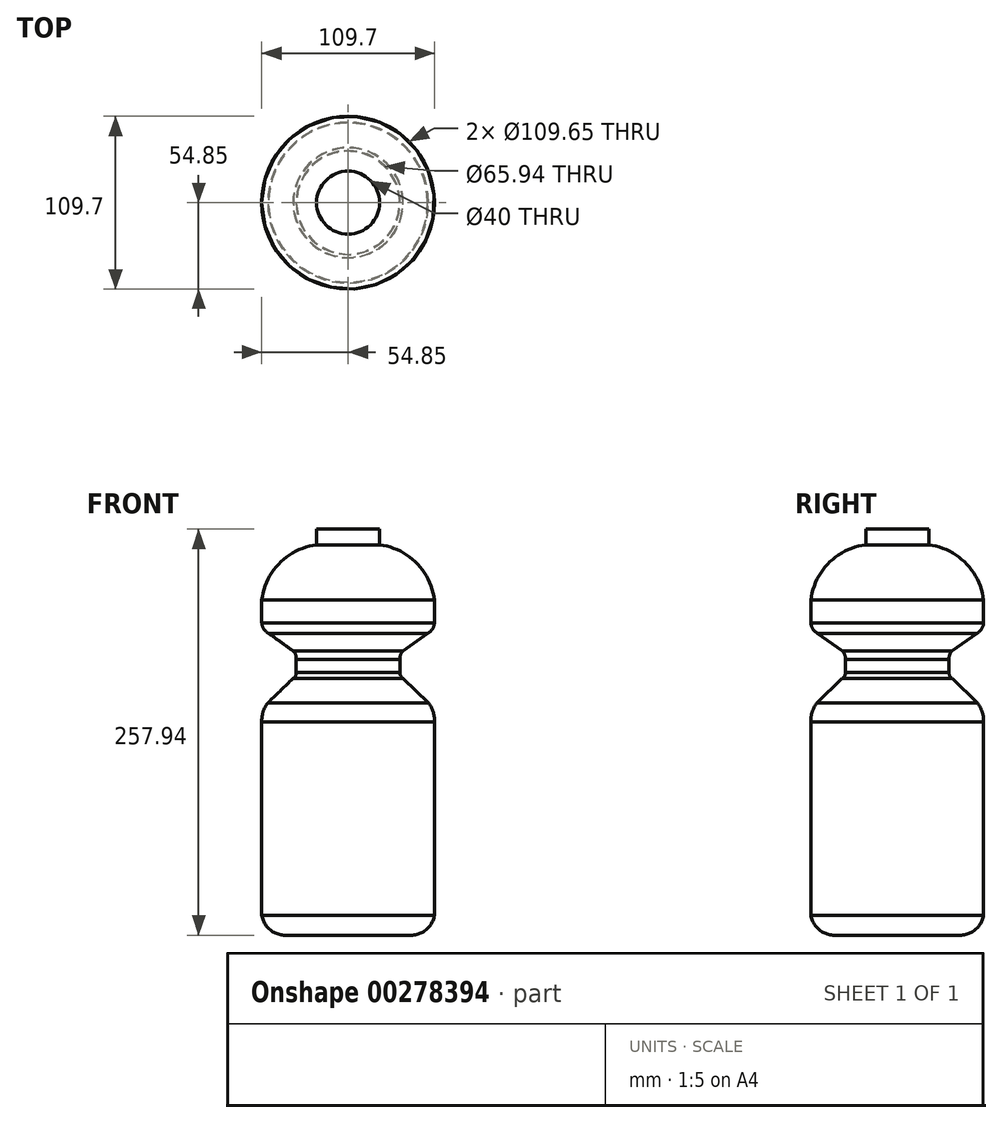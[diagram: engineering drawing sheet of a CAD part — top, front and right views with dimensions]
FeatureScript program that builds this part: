
annotation { "Feature Type Name" : "Feature", "Feature Type Description" : "" }
export const myFeature = defineFeature(function(context is Context, id is Id, definition is map)
    precondition{}
    {
        {
            var Q0;
            Q0=qCreatedBy(makeId("Front.planeOp"),FACE);
            var sketch = newSketch(context, id + "F0", { "sketchPlane" : qUnion([Q0])});
            skLineSegment(sketch, "E0", {"start": v(0, -131.27) * mm, "end": v(40, -131.27) * mm});
            skArc(sketch, "E1", {"start": v(40, -131.27) * mm, "mid": v(49.77, -127.65) * mm, "end": v(54.83, -118.55) * mm});
            skArc(sketch, "E2", {"start": v(54.83, 81.63) * mm, "mid": v(43.47, 105.17) * mm, "end": v(20, 116.67) * mm});
            skLineSegment(sketch, "E3", {"start": v(20, 116.67) * mm, "end": v(20, 126.67) * mm});
            skArc(sketch, "E4", {"start": v(50.53, 60.47) * mm, "mid": v(53.5, 63.2) * mm, "end": v(54.83, 67.02) * mm});
            skArc(sketch, "E5", {"start": v(34.73, 49.16) * mm, "mid": v(33.27, 46.76) * mm, "end": v(32.97, 43.97) * mm});
            skLineSegment(sketch, "E6", {"start": v(34.73, 49.16) * mm, "end": v(50.53, 60.47) * mm});
            skLineSegment(sketch, "E7", {"start": v(54.83, 67.02) * mm, "end": v(54.83, 81.63) * mm});
            skArc(sketch, "E8", {"start": v(32.97, 35.69) * mm, "mid": v(33.38, 33.43) * mm, "end": v(35, 31.8) * mm});
            skLineSegment(sketch, "E9", {"start": v(32.97, 43.97) * mm, "end": v(32.97, 35.69) * mm});
            skArc(sketch, "E10", {"start": v(54.83, 4.22) * mm, "mid": v(54, 10.61) * mm, "end": v(50.97, 16.3) * mm});
            skLineSegment(sketch, "E11", {"start": v(35, 31.8) * mm, "end": v(50.97, 16.3) * mm});
            skLineSegment(sketch, "E12", {"start": v(54.83, 4.22) * mm, "end": v(54.83, -118.55) * mm});
            skSolve(sketch);
        }
        {
            var Q0;
            Q0=qCreatedBy(makeId("Front.planeOp"),FACE);
            var sketch = newSketch(context, id + "F1", { "sketchPlane" : qUnion([Q0])});
            skLineSegment(sketch, "E13", {"start": v(0, 43.58) * mm, "end": v(0, -33) * mm});
            skSolve(sketch);
        }
        {
            var Q0;
            Q0 = qSketchRegion(id + "F0", true);
            var Q1;
            Q1=sQuery(id+"F0.wireOp",EDGE,"ZKri3n2W-re8a-1k9S-9Pg9-qm2uIruXetHU");
            var Q2;
            Q2=sQuery(id+"F0.wireOp",EDGE,"726038e4-92dc-4729-8b95-717d3ab76cc9");
            var Q3;
            Q3=sQuery(id+"F0.wireOp",EDGE,"RCTSUEqe-3Uja-wSTD-oBcY-UVFVVT68YvoV");
            var Q4;
            Q4=sQuery(id+"F0.wireOp",EDGE,"b73a519c-e8e9-420d-b65a-1e53ab4c0354");
            var Q5;
            Q5=sQuery(id+"F0.wireOp",EDGE,"71482556-2425-4c6e-8db7-28dbb01381e5");
            var Q6;
            Q6=sQuery(id+"F0.wireOp",EDGE,"E3");
            var Q7;
            Q7=sQuery(id+"F0.wireOp",EDGE,"E2");
            var Q8;
            Q8=sQuery(id+"F0.wireOp",EDGE,"E7");
            var Q9;
            Q9=sQuery(id+"F0.wireOp",EDGE,"E6");
            var Q10;
            Q10=sQuery(id+"F0.wireOp",EDGE,"E4");
            var Q11;
            Q11=sQuery(id+"F0.wireOp",EDGE,"E9");
            var Q12;
            Q12=sQuery(id+"F0.wireOp",EDGE,"E5");
            var Q13;
            Q13=sQuery(id+"F0.wireOp",EDGE,"E8");
            var Q14;
            Q14=sQuery(id+"F0.wireOp",EDGE,"E11");
            var Q15;
            Q15=sQuery(id+"F0.wireOp",EDGE,"E10");
            var Q16;
            Q16=sQuery(id+"F0.wireOp",EDGE,"E12");
            var Q17;
            Q17=sQuery(id+"F0.wireOp",EDGE,"E1");
            var Q18;
            Q18=sQuery(id+"F0.wireOp",EDGE,"E0");
            var Q19;
            Q19=sQuery(id+"F1.wireOp",EDGE,"E13");
            revolve(context, id + "F2", {"bodyType" : ToolBodyType.SURFACE, "surfaceOperationType" : NewSurfaceOperationType.NEW, "entities" : qUnion([Q0]), "surfaceEntities" : qUnion([Q1, Q2, Q3, Q4, Q5, Q6, Q7, Q8, Q9, Q10, Q11, Q12, Q13, Q14, Q15, Q16, Q17, Q18]), "axis" : qUnion([Q19]), "revolveType" : RevolveType.FULL});
        }
    });
